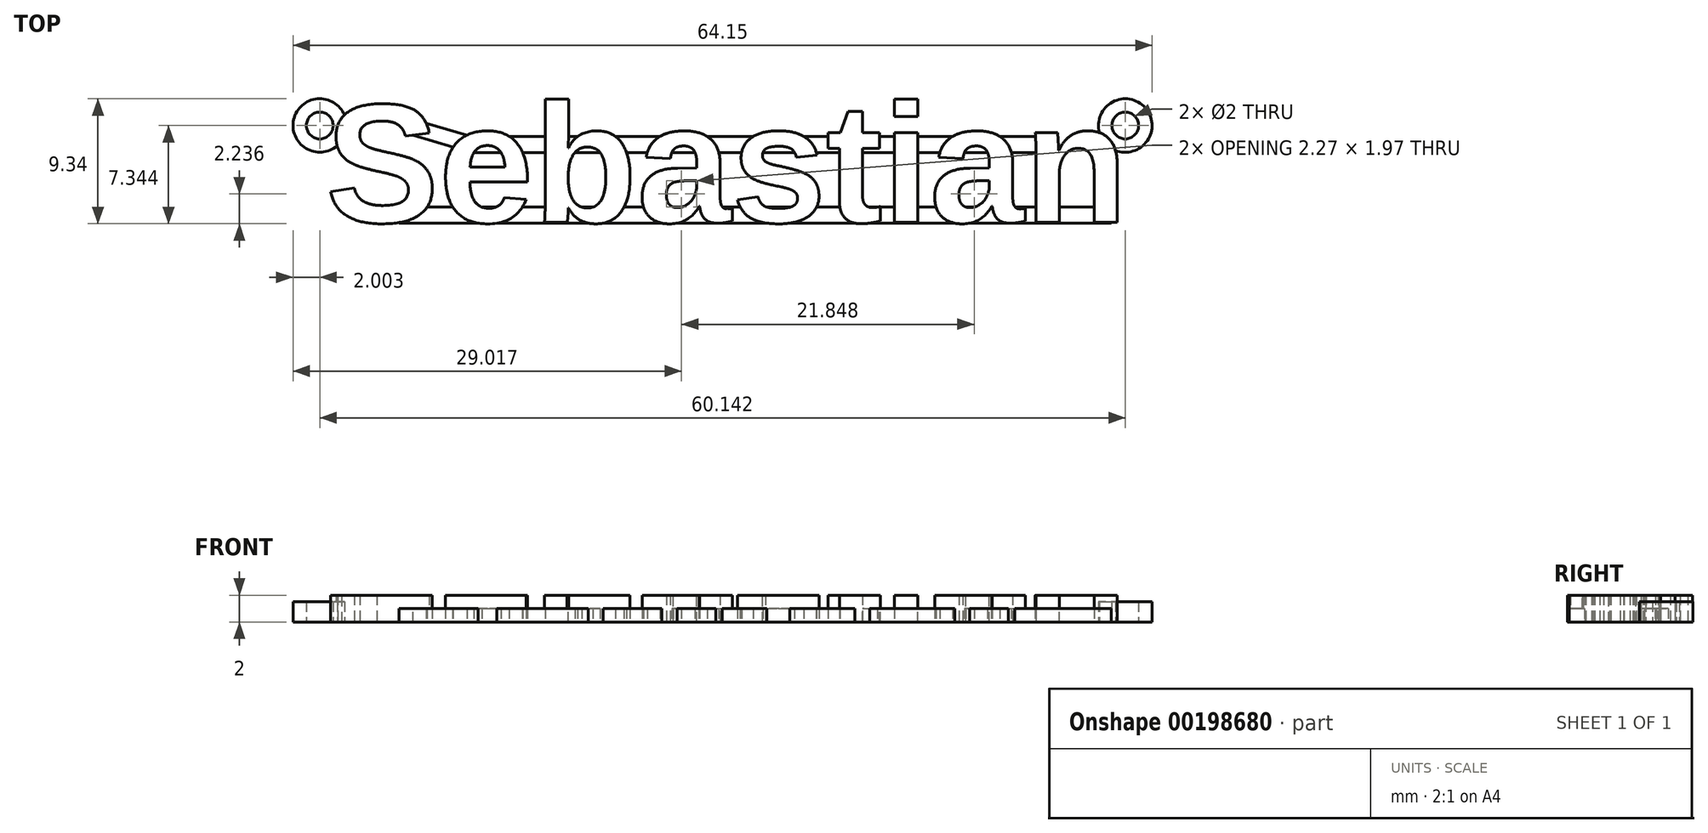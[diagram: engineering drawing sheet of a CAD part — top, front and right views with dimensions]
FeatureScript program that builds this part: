
annotation { "Feature Type Name" : "Feature", "Feature Type Description" : "" }
export const myFeature = defineFeature(function(context is Context, id is Id, definition is map)
    precondition{}
    {
        {
            var Q0;
            Q0=qCreatedBy(makeId("Top.planeOp"),FACE);
            var sketch = newSketch(context, id + "F0", { "sketchPlane" : qUnion([Q0])});
            skText(sketch, "E0", { "text": "Sebastian", "fontName": "Arimo-Bold.ttf"});
            const initialGuessF0  = {"E0": [-0.02416, 0.00163, 1, 0, 0.00913]};
            skSetInitialGuess(sketch, initialGuessF0);
            skSolve(sketch);
        }
        {
            var Q0;
            Q0=makeQuery(id+"F0.imprint","IMPRINT",FACE,{"disambiguationData":[TD([[makeQuery(id+"F0.imprint","IMPRINT",EDGE,{"derivedFrom":sQuery(id+"F0.wireOp",EDGE,"E0.sketch_text.stroke-0")}),-1.0]])]});
            var sketch = newSketch(context, id + "F1", { "sketchPlane" : qUnion([Q0])});
            skCircle(sketch, "E1", {"center": v(-24.6, 8.85) * mm, "radius": 2 * mm});
            skCircle(sketch, "E2", {"center": v(-24.6, 8.85) * mm, "radius": 1 * mm});
            skCircle(sketch, "E3", {"center": v(35.55, 8.85) * mm, "radius": 2 * mm});
            skCircle(sketch, "E4", {"center": v(35.55, 8.85) * mm, "radius": 1 * mm});
            skLineSegment(sketch, "E5.bottom", {"start": v(-13.27, 8.04) * mm, "end": v(29.47, 8.04) * mm});
            skLineSegment(sketch, "E5.top", {"start": v(-13.27, 6.84) * mm, "end": v(29.47, 6.84) * mm});
            skLineSegment(sketch, "E5.left", {"start": v(-13.27, 8.04) * mm, "end": v(-13.27, 6.84) * mm});
            skLineSegment(sketch, "E5.right", {"start": v(29.47, 8.04) * mm, "end": v(29.47, 6.84) * mm});
            skLineSegment(sketch, "E6.bottom", {"start": v(-18.68, 2.76) * mm, "end": v(34.49, 2.76) * mm});
            skLineSegment(sketch, "E6.top", {"start": v(-18.68, 1.56) * mm, "end": v(34.49, 1.56) * mm});
            skLineSegment(sketch, "E6.left", {"start": v(-18.68, 2.76) * mm, "end": v(-18.68, 1.56) * mm});
            skLineSegment(sketch, "E6.right", {"start": v(34.49, 2.76) * mm, "end": v(34.49, 1.56) * mm});
            skLineSegment(sketch, "E7", {"start": v(-13.27, 8.04) * mm, "end": v(-17.05, 9.14) * mm});
            skLineSegment(sketch, "E8", {"start": v(-17.05, 9.14) * mm, "end": v(-17.8, 8.19) * mm});
            skLineSegment(sketch, "E9", {"start": v(-17.8, 8.19) * mm, "end": v(-13.27, 6.84) * mm});
            skSolve(sketch);
        }
        {
            var Q0;
            Q0=qSketchRegion(id+"F0",true);
            extrude(context, id + "F2", {"entities" : qUnion([Q0]), "depth" : 2 * mm});
        }
        {
            var Q0;
            Q0=qSketchRegion(id+"F1",true);
            extrude(context, id + "F3", {"entities" : qUnion([Q0]), "operationType" : NewBodyOperationType.ADD, "depth" : 1 * mm});
        }
        {
            var Q0;
            Q0=makeQuery(id+"F1.imprint","IMPRINT",FACE,{"disambiguationData":[TD([[makeQuery(id+"F1.imprint","IMPRINT",EDGE,{"derivedFrom":sQuery(id+"F1.wireOp",EDGE,"E2")}),-1.0]])]});
            var Q1;
            Q1=makeQuery(id+"F1.imprint","IMPRINT",FACE,{"disambiguationData":[TD([[makeQuery(id+"F1.imprint","IMPRINT",EDGE,{"derivedFrom":sQuery(id+"F1.wireOp",EDGE,"E3")}),1.0]])]});
            extrude(context, id + "F4", {"entities" : qUnion([Q0, Q1]), "operationType" : NewBodyOperationType.ADD, "depth" : 1.5 * mm});
        }
    });
